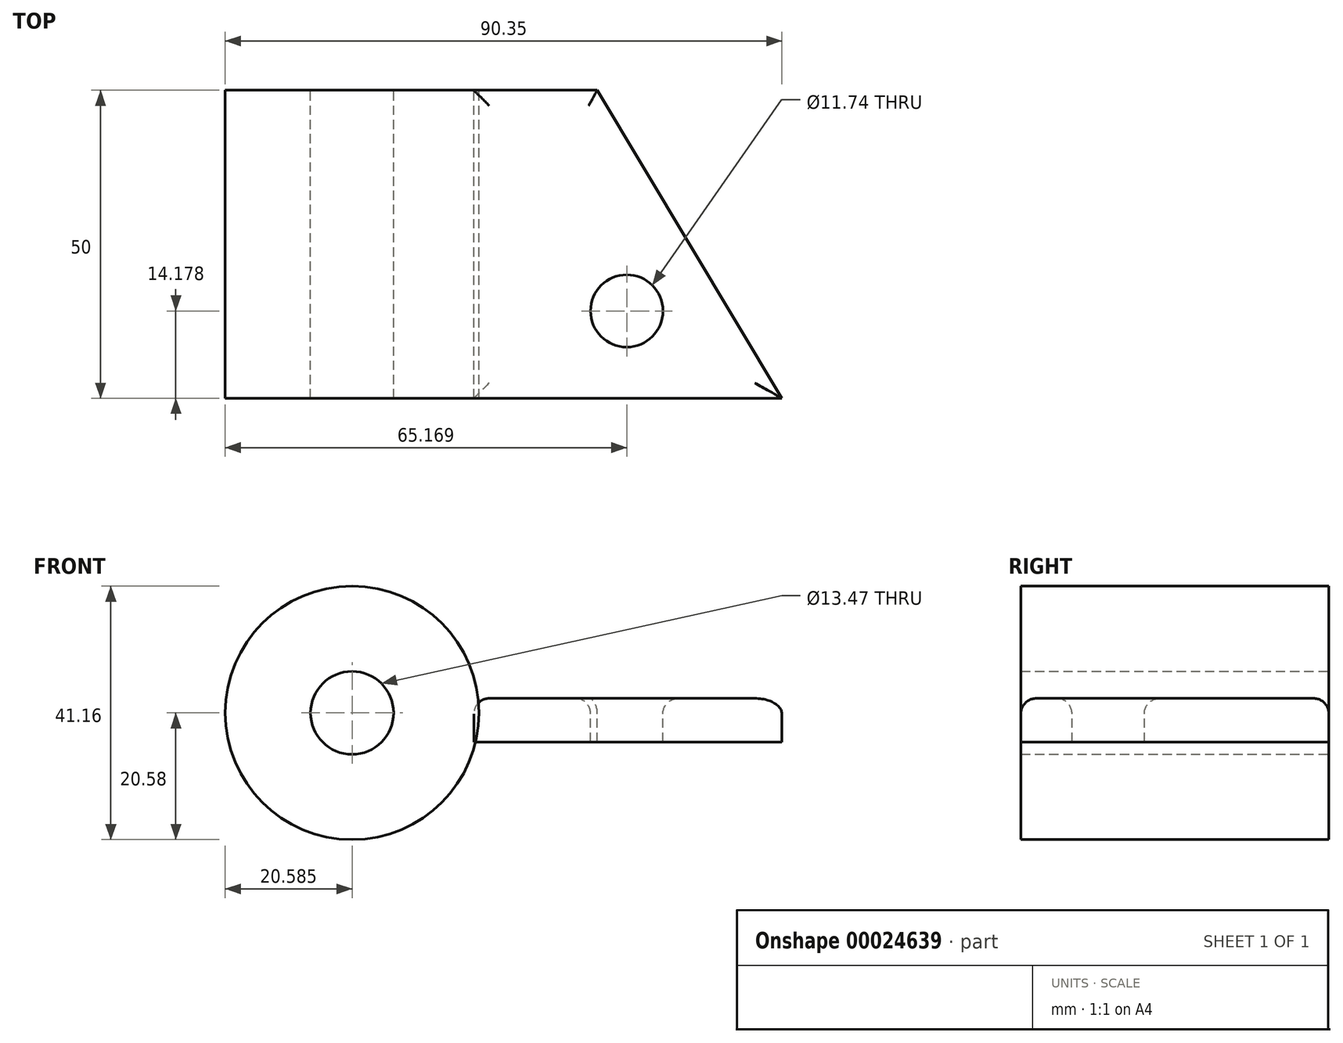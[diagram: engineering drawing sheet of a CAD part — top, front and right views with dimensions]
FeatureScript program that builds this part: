
annotation { "Feature Type Name" : "Feature", "Feature Type Description" : "" }
export const myFeature = defineFeature(function(context is Context, id is Id, definition is map)
    precondition{}
    {
        {
            var Q0;
            Q0=qCreatedBy(makeId("Front.planeOp"),FACE);
            var sketch = newSketch(context, id + "F0", { "sketchPlane" : qUnion([Q0])});
            skCircle(sketch, "E0", {"center": v(-44.76, 6.82) * mm, "radius": 20.58 * mm});
            skCircle(sketch, "E1", {"center": v(-44.76, 6.82) * mm, "radius": 6.74 * mm});
            skSolve(sketch);
        }
        {
            var Q0;
            Q0=makeQuery(id+"F0.imprint","IMPRINT",FACE,{"disambiguationData":[TD([[makeQuery(id+"F0.imprint","IMPRINT",EDGE,{"derivedFrom":sQuery(id+"F0.wireOp",EDGE,"E0")}),1.0]])]});
            extrude(context, id + "F1", {"entities" : qUnion([Q0]), "depth" : 50 * mm});
        }
        {
            var Q0;
            Q0=qCreatedBy(makeId("Right.planeOp"),FACE);
            var sketch = newSketch(context, id + "F2", { "sketchPlane" : qUnion([Q0])});
            skLineSegment(sketch, "E2.bottom", {"start": v(-50.14, 9.18) * mm, "end": v(0, 9.18) * mm});
            skLineSegment(sketch, "E2.top", {"start": v(-50.14, 2.1) * mm, "end": v(0, 2.1) * mm});
            skLineSegment(sketch, "E2.left", {"start": v(-50.14, 9.18) * mm, "end": v(-50.14, 2.1) * mm});
            skLineSegment(sketch, "E2.right", {"start": v(0, 9.18) * mm, "end": v(0, 2.1) * mm});
            skSolve(sketch);
        }
        {
            var Q0;
            Q0=makeQuery(id+"F2.imprint","IMPRINT",FACE,{"disambiguationData":[TD([[makeQuery(id+"F2.imprint","IMPRINT",EDGE,{"derivedFrom":sQuery(id+"F2.wireOp",EDGE,"E2.bottom")}),-1.0]])]});
            extrude(context, id + "F3", {"entities" : qUnion([Q0]), "oppositeDirection" : true, "depth" : 25 * mm});
        }
        {
            var Q0;
            Q0=makeQuery(id+"F3.opExtrude","CAP_FACE",FACE,{"disambiguationData":[OSD([sQuery(id+"F2.wireOp",EDGE,"E2.bottom"),sQuery(id+"F2.wireOp",EDGE,"E2.top"),sQuery(id+"F2.wireOp",EDGE,"E2.left"),sQuery(id+"F2.wireOp",EDGE,"E2.right")])],"isStart":true});
            extrude(context, id + "F4", {"entities" : qUnion([Q0]), "operationType" : NewBodyOperationType.ADD, "depth" : 25 * mm});
        }
        {
            var Q0;
            {var subQ0=sQuery(id+"F2.wireOp",EDGE,"E2.left");Q0=makeQuery(id+"F4.boolean.opBoolean","MERGE",FACE,{"derivedFrom":[makeQuery(id+"F3.opExtrude","SWEPT_FACE",FACE,{"disambiguationData":[OSD([subQ0])]}),makeQuery(id+"F4.opExtrude","SWEPT_FACE",FACE,{"disambiguationData":[OSD([subQ0])]})]});}
            var Q1;
            Q1=makeQuery(id+"F1.opExtrude","CAP_FACE",FACE,{"disambiguationData":[OSD([sQuery(id+"F0.wireOp",EDGE,"E0"),sQuery(id+"F0.wireOp",EDGE,"E1")])],"isStart":false});
            extrude(context, id + "F5", {"entities" : qUnion([Q0]), "operationType" : NewBodyOperationType.REMOVE, "endBound" : BoundingType.UP_TO_SURFACE, "oppositeDirection" : true, "endBoundEntityFace" : qUnion([Q1]), "depth" : 25 * mm});
        }
        {
            var Q0;
            {var subQ0=sQuery(id+"F2.wireOp",EDGE,"E2.bottom");Q0=makeQuery(id+"F4.boolean.opBoolean","MERGE",FACE,{"derivedFrom":[makeQuery(id+"F3.opExtrude","SWEPT_FACE",FACE,{"disambiguationData":[OSD([subQ0])]}),makeQuery(id+"F4.opExtrude","SWEPT_FACE",FACE,{"disambiguationData":[OSD([subQ0])]})]});}
            var sketch = newSketch(context, id + "F6", { "sketchPlane" : qUnion([Q0])});
            skLineSegment(sketch, "E3", {"start": v(25, -50) * mm, "end": v(-4.96, 0) * mm});
            skSolve(sketch);
        }
        {
            var Q0;
            {var subQ3=sQuery(id+"F6.wireOp",EDGE,"E3");Q0=makeQuery(id+"F6.imprint","IMPRINT",FACE,{"disambiguationData":[TD([[makeQuery(id+"F6.imprint","IMPRINT",EDGE,{"derivedFrom":subQ3}),-1.0]])]});}
            extrude(context, id + "F7", {"entities" : qUnion([Q0]), "operationType" : NewBodyOperationType.REMOVE, "endBound" : BoundingType.THROUGH_ALL, "oppositeDirection" : true, "depth" : 25 * mm});
        }
        {
            var Q0;
            {var subQ0=sQuery(id+"F2.wireOp",EDGE,"E2.bottom");Q0=makeQuery(id+"F4.boolean.opBoolean","MERGE",FACE,{"derivedFrom":[makeQuery(id+"F3.opExtrude","SWEPT_FACE",FACE,{"disambiguationData":[OSD([subQ0])]}),makeQuery(id+"F4.opExtrude","SWEPT_FACE",FACE,{"disambiguationData":[OSD([subQ0])]})]});}
            var sketch = newSketch(context, id + "F8", { "sketchPlane" : qUnion([Q0])});
            skCircle(sketch, "E4", {"center": v(-0.18, -35.82) * mm, "radius": 5.87 * mm});
            skSolve(sketch);
        }
        {
            var Q0;
            Q0=makeQuery(id+"F8.imprint","IMPRINT",FACE,{"disambiguationData":[TD([[makeQuery(id+"F8.imprint","IMPRINT",EDGE,{"derivedFrom":sQuery(id+"F8.wireOp",EDGE,"E4")}),1.0]])]});
            extrude(context, id + "F9", {"entities" : qUnion([Q0]), "operationType" : NewBodyOperationType.REMOVE, "endBound" : BoundingType.THROUGH_ALL, "oppositeDirection" : true, "depth" : 25 * mm});
        }
        {
            var Q0;
            {var subQ0=sQuery(id+"F2.wireOp",EDGE,"E2.bottom");Q0=makeQuery(id+"F4.boolean.opBoolean","MERGE",FACE,{"derivedFrom":[makeQuery(id+"F3.opExtrude","SWEPT_FACE",FACE,{"disambiguationData":[OSD([subQ0])]}),makeQuery(id+"F4.opExtrude","SWEPT_FACE",FACE,{"disambiguationData":[OSD([subQ0])]})]});}
            fillet(context, id + "F10", {"entities" : qUnion([Q0]), "radius" : 2.5 * mm, "tangentPropagation" : true, "allowEdgeOverflow" : false});
        }
    });
